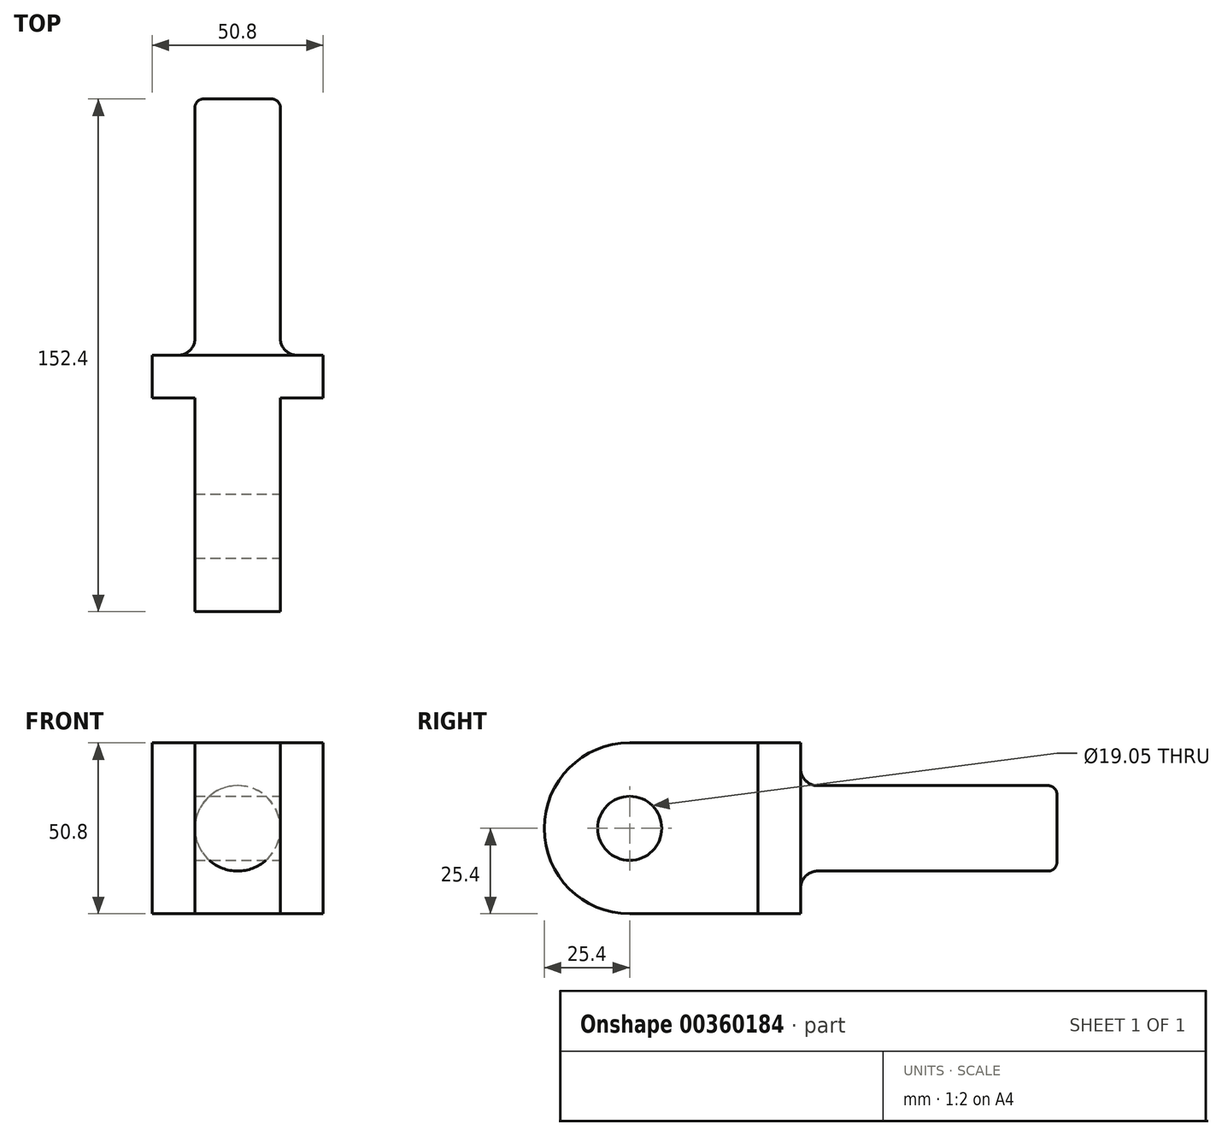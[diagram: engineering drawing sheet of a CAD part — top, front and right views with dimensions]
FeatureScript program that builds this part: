
annotation { "Feature Type Name" : "Feature", "Feature Type Description" : "" }
export const myFeature = defineFeature(function(context is Context, id is Id, definition is map)
    precondition{}
    {
        {
            var Q0;
            Q0=qCreatedBy(makeId("Front.planeOp"),FACE);
            var sketch = newSketch(context, id + "F0", { "sketchPlane" : qUnion([Q0])});
            skLineSegment(sketch, "E0.bottom", {"start": v(0, 0) * mm, "end": v(50.8, 0) * mm});
            skLineSegment(sketch, "E0.top", {"start": v(0, 50.8) * mm, "end": v(50.8, 50.8) * mm});
            skLineSegment(sketch, "E0.left", {"start": v(0, 0) * mm, "end": v(0, 50.8) * mm});
            skLineSegment(sketch, "E0.right", {"start": v(50.8, 0) * mm, "end": v(50.8, 50.8) * mm});
            skSolve(sketch);
        }
        {
            var Q0;
            Q0 = qSketchRegion(id + "F0", true);
            extrude(context, id + "F1", {"entities" : qUnion([Q0]), "depth" : 12.7 * mm});
        }
        {
            var Q0;
            Q0=makeQuery(id+"F1.opExtrude","CAP_FACE",FACE,{"disambiguationData":[OSD([sQuery(id+"F0.wireOp",EDGE,"E0.bottom"),sQuery(id+"F0.wireOp",EDGE,"E0.top"),sQuery(id+"F0.wireOp",EDGE,"E0.left"),sQuery(id+"F0.wireOp",EDGE,"E0.right")])],"isStart":false});
            var sketch = newSketch(context, id + "F2", { "sketchPlane" : qUnion([Q0])});
            skLineSegment(sketch, "E1", {"start": v(25.4, 50.8) * mm, "end": v(25.4, 0) * mm, "construction": true});
            skLineSegment(sketch, "E2.bottom", {"start": v(25.4, 50.8) * mm, "end": v(12.7, 50.8) * mm});
            skLineSegment(sketch, "E2.top", {"start": v(25.4, 0) * mm, "end": v(12.7, 0) * mm});
            skLineSegment(sketch, "E2.left", {"start": v(25.4, 50.8) * mm, "end": v(25.4, 0) * mm});
            skLineSegment(sketch, "E2.right", {"start": v(12.7, 50.8) * mm, "end": v(12.7, 0) * mm});
            skLineSegment(sketch, "E3.bottom", {"start": v(25.4, 50.8) * mm, "end": v(38.1, 50.8) * mm});
            skLineSegment(sketch, "E3.top", {"start": v(25.4, 0) * mm, "end": v(38.1, 0) * mm});
            skLineSegment(sketch, "E3.right", {"start": v(38.1, 50.8) * mm, "end": v(38.1, 0) * mm});
            skSolve(sketch);
        }
        {
            var Q0;
            Q0 = qSketchRegion(id + "F2", true);
            extrude(context, id + "F3", {"entities" : qUnion([Q0]), "operationType" : NewBodyOperationType.ADD, "depth" : 38.1 * mm});
        }
        {
            var Q0;
            Q0=makeQuery(id+"F3.opExtrude","SWEPT_FACE",FACE,{"disambiguationData":[OSD([sQuery(id+"F2.wireOp",EDGE,"E3.right")])]});
            var sketch = newSketch(context, id + "F4", { "sketchPlane" : qUnion([Q0])});
            skArc(sketch, "E4", {"start": v(-50.8, 50.8) * mm, "mid": v(-76.2, 25.4) * mm, "end": v(-50.8, 0) * mm});
            skLineSegment(sketch, "E5", {"start": v(-50.8, 50.8) * mm, "end": v(-50.8, 0) * mm});
            skSolve(sketch);
        }
        {
            var Q0;
            Q0 = qSketchRegion(id + "F4", true);
            extrude(context, id + "F5", {"entities" : qUnion([Q0]), "operationType" : NewBodyOperationType.ADD, "oppositeDirection" : true, "depth" : 25.4 * mm});
        }
        {
            var Q0;
            Q0=makeQuery(id+"F5.boolean.opBoolean","MERGE",FACE,{"derivedFrom":[makeQuery(id+"F3.opExtrude","SWEPT_FACE",FACE,{"disambiguationData":[OSD([sQuery(id+"F2.wireOp",EDGE,"E3.right")])]}),makeQuery(id+"F5.opExtrude","CAP_FACE",FACE,{"disambiguationData":[OSD([sQuery(id+"F4.wireOp",EDGE,"E4"),sQuery(id+"F4.wireOp",EDGE,"E5")])],"isStart":true})]});
            var sketch = newSketch(context, id + "F6", { "sketchPlane" : qUnion([Q0])});
            skCircle(sketch, "E6", {"center": v(-50.8, 25.4) * mm, "radius": 9.53 * mm});
            skSolve(sketch);
        }
        {
            var Q0;
            Q0 = qSketchRegion(id + "F6", true);
            extrude(context, id + "F7", {"entities" : qUnion([Q0]), "operationType" : NewBodyOperationType.REMOVE, "oppositeDirection" : true, "depth" : 25.4 * mm});
        }
        {
            var Q0;
            Q0=makeQuery(id+"F1.opExtrude","CAP_FACE",FACE,{"disambiguationData":[OSD([sQuery(id+"F0.wireOp",EDGE,"E0.bottom"),sQuery(id+"F0.wireOp",EDGE,"E0.top"),sQuery(id+"F0.wireOp",EDGE,"E0.left"),sQuery(id+"F0.wireOp",EDGE,"E0.right")])],"isStart":true});
            var sketch = newSketch(context, id + "F8", { "sketchPlane" : qUnion([Q0])});
            skLineSegment(sketch, "E7.bottom", {"start": v(-50.8, 50.8) * mm, "end": v(0, 50.8) * mm, "construction": true});
            skLineSegment(sketch, "E7.top", {"start": v(-50.8, 0) * mm, "end": v(0, 0) * mm, "construction": true});
            skLineSegment(sketch, "E7.left", {"start": v(-50.8, 50.8) * mm, "end": v(-50.8, 0) * mm, "construction": true});
            skLineSegment(sketch, "E7.right", {"start": v(0, 50.8) * mm, "end": v(0, 0) * mm, "construction": true});
            skLineSegment(sketch, "E8", {"start": v(-50.8, 50.8) * mm, "end": v(0, 0) * mm, "construction": true});
            skLineSegment(sketch, "E9", {"start": v(0, 50.8) * mm, "end": v(-50.8, 0) * mm, "construction": true});
            skCircle(sketch, "E10", {"center": v(-25.4, 25.4) * mm, "radius": 12.7 * mm});
            skSolve(sketch);
        }
        {
            var Q0;
            Q0 = qSketchRegion(id + "F8", true);
            extrude(context, id + "F9", {"entities" : qUnion([Q0]), "operationType" : NewBodyOperationType.ADD, "depth" : 76.2 * mm});
        }
        {
            var Q0;
            Q0=makeQuery(id+"F9.opExtrude","CAP_FACE",FACE,{"disambiguationData":[OSD([sQuery(id+"F8.wireOp",EDGE,"E10")])],"isStart":false});
            fillet(context, id + "F10", {"entities" : qUnion([Q0]), "radius" : 2.54 * mm, "tangentPropagation" : true, "allowEdgeOverflow" : false});
        }
        {
            var Q0;
            Q0=makeQuery(id+"F9.opExtrude","SWEPT_FACE",FACE,{"disambiguationData":[OSD([sQuery(id+"F8.wireOp",EDGE,"E10")])]});
            fillet(context, id + "F11", {"entities" : qUnion([Q0]), "radius" : 5.08 * mm, "tangentPropagation" : true, "allowEdgeOverflow" : false});
        }
    });
